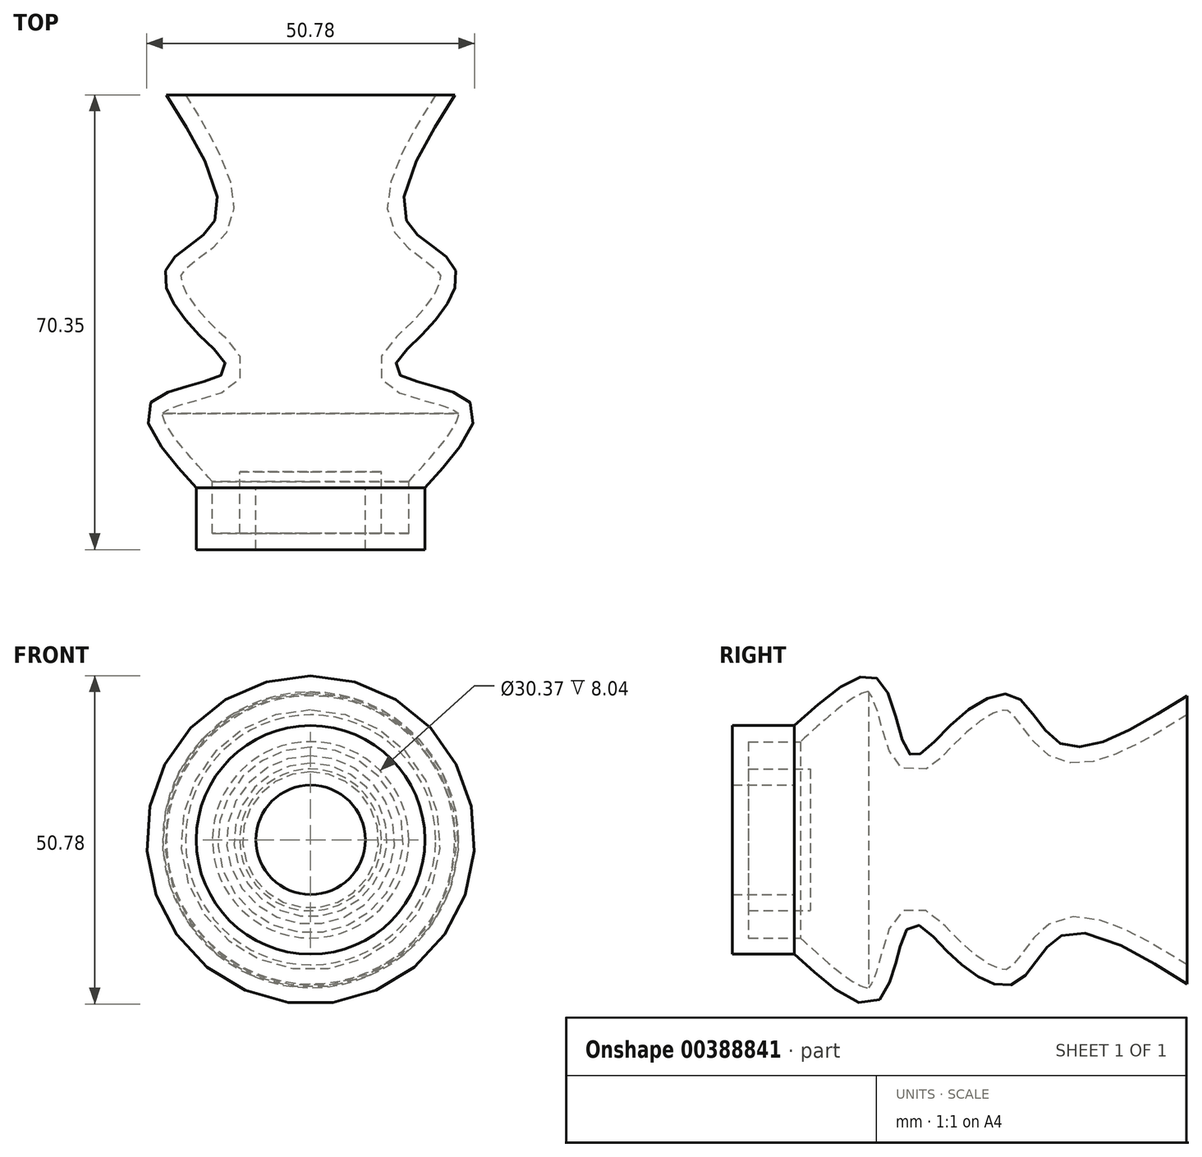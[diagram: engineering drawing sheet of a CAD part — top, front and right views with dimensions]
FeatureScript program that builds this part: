
annotation { "Feature Type Name" : "Feature", "Feature Type Description" : "" }
export const myFeature = defineFeature(function(context is Context, id is Id, definition is map)
    precondition{}
    {
        {
            var Q0;
            Q0=qCreatedBy(makeId("Top.planeOp"),FACE);
            var sketch = newSketch(context, id + "F0", { "sketchPlane" : qUnion([Q0])});
            skLineSegment(sketch, "E0", {"start": v(0, 0) * mm, "end": v(0, -60.77) * mm});
            skLineSegment(sketch, "E1", {"start": v(0, -60.77) * mm, "end": v(8.47, -60.77) * mm});
            skLineSegment(sketch, "E2", {"start": v(8.47, -60.77) * mm, "end": v(8.47, -70.35) * mm});
            skLineSegment(sketch, "E3", {"start": v(8.47, -70.35) * mm, "end": v(17.69, -70.35) * mm});
            skLineSegment(sketch, "E4", {"start": v(17.69, -70.35) * mm, "end": v(17.69, -60.77) * mm});
            skLineSegment(sketch, "E5", {"start": v(0, 0) * mm, "end": v(22.3, 0) * mm});
            skFitSpline(sketch, "E6", {"points": [v(22.3, 0) * mm, v(14.85, -19.46) * mm, v(22.3, -26.73) * mm, v(17.69, -36.66) * mm, v(13.25, -42.87) * mm, v(24.78, -47.65) * mm, v(17.69, -60.77) * mm], "startDerivative": vector(-66.3, -105.4) * mm, "endDerivative": vector(-77.69, -85.53) * mm});
            skSolve(sketch);
        }
        {
            var Q0;
            Q0 = qSketchRegion(id + "F0", true);
            var Q1;
            Q1=sQuery(id+"F0.wireOp",EDGE,"E0");
            revolve(context, id + "F1", {"entities" : qUnion([Q0]), "axis" : qUnion([Q1]), "revolveType" : RevolveType.FULL});
        }
        {
            var Q0;
            Q0=makeQuery(id+"F1.opRevolve","SWEPT_FACE",FACE,{"disambiguationData":[OSD([sQuery(id+"F0.wireOp",EDGE,"E5")])]});
            shell(context, id + "F2", {"entities" : qUnion([Q0]), "thickness" : 2.5 * mm});
        }
    });
